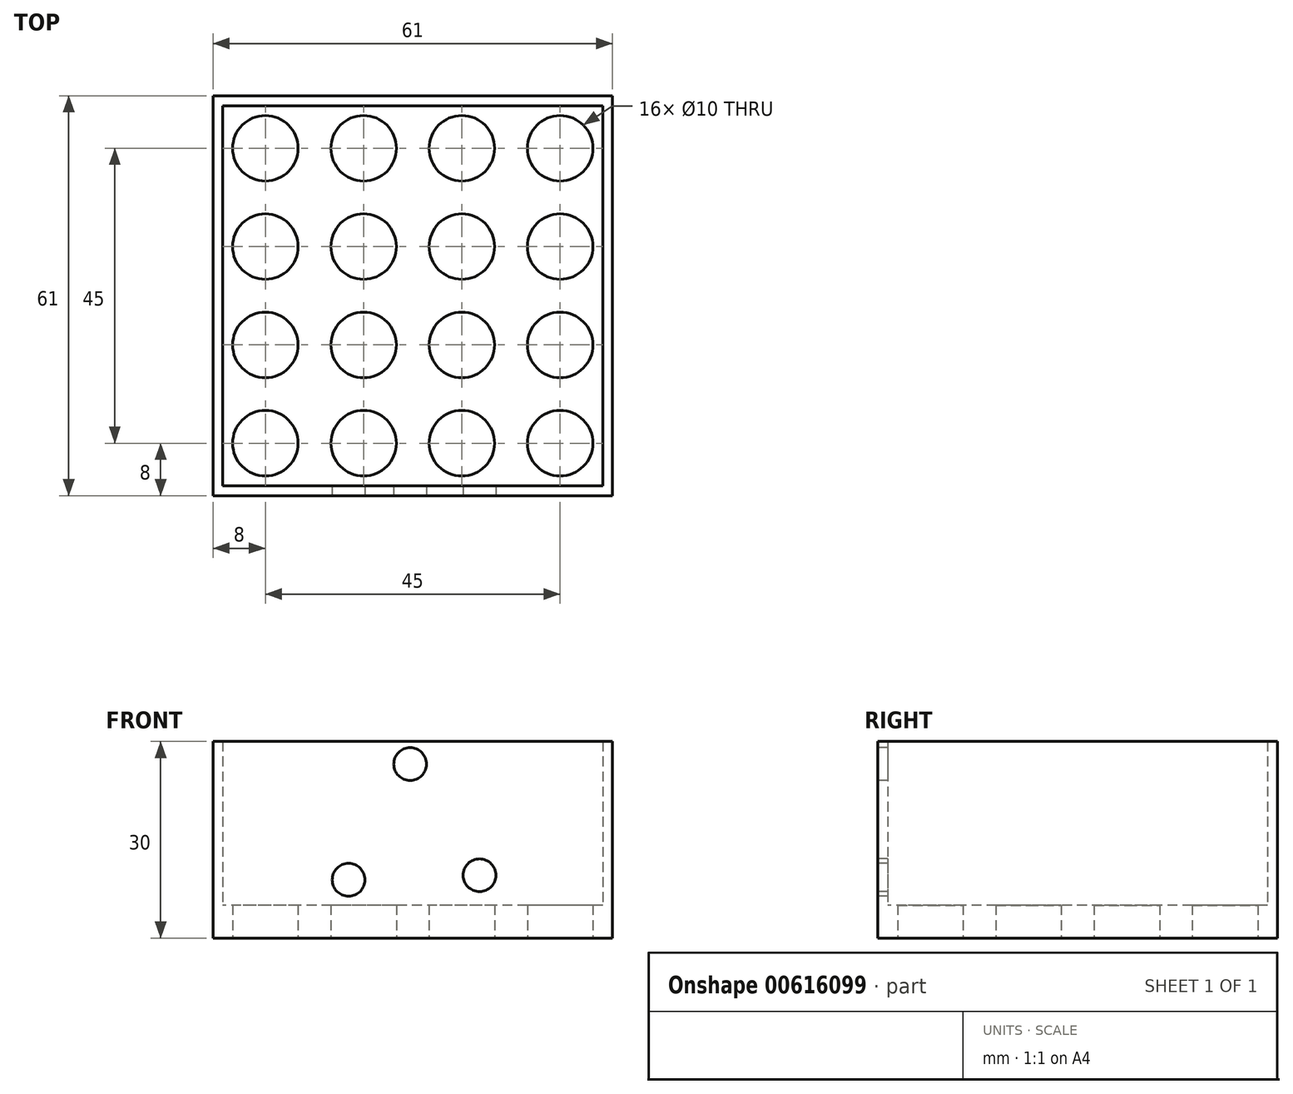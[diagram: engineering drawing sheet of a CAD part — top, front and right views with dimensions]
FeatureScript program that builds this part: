
annotation { "Feature Type Name" : "Feature", "Feature Type Description" : "" }
export const myFeature = defineFeature(function(context is Context, id is Id, definition is map)
    precondition{}
    {
        {
            var Q0;
            Q0=qCreatedBy(makeId("Top.planeOp"),FACE);
            var sketch = newSketch(context, id + "F0", { "sketchPlane" : qUnion([Q0])});
            skCircle(sketch, "E0", {"center": v(0, 0) * mm, "radius": 5 * mm});
            skCircle(sketch, "E1.0.1.0", {"center": v(0, 15) * mm, "radius": 5 * mm});
            skCircle(sketch, "E1.0.2.0", {"center": v(0, 30) * mm, "radius": 5 * mm});
            skCircle(sketch, "E1.0.3.0", {"center": v(0, 45) * mm, "radius": 5 * mm});
            skCircle(sketch, "E1.1.0.0", {"center": v(15, 0) * mm, "radius": 5 * mm});
            skCircle(sketch, "E1.1.1.0", {"center": v(15, 15) * mm, "radius": 5 * mm});
            skCircle(sketch, "E1.1.2.0", {"center": v(15, 30) * mm, "radius": 5 * mm});
            skCircle(sketch, "E1.1.3.0", {"center": v(15, 45) * mm, "radius": 5 * mm});
            skCircle(sketch, "E1.2.0.0", {"center": v(30, 0) * mm, "radius": 5 * mm});
            skCircle(sketch, "E1.2.1.0", {"center": v(30, 15) * mm, "radius": 5 * mm});
            skCircle(sketch, "E1.2.2.0", {"center": v(30, 30) * mm, "radius": 5 * mm});
            skCircle(sketch, "E1.2.3.0", {"center": v(30, 45) * mm, "radius": 5 * mm});
            skCircle(sketch, "E1.3.0.0", {"center": v(45, 0) * mm, "radius": 5 * mm});
            skCircle(sketch, "E1.3.1.0", {"center": v(45, 15) * mm, "radius": 5 * mm});
            skCircle(sketch, "E1.3.2.0", {"center": v(45, 30) * mm, "radius": 5 * mm});
            skCircle(sketch, "E1.3.3.0", {"center": v(45, 45) * mm, "radius": 5 * mm});
            skLineSegment(sketch, "E1.direction1", {"start": v(0, 0) * mm, "end": v(15, 0) * mm, "construction": true});
            skLineSegment(sketch, "E1.direction2", {"start": v(0, 0) * mm, "end": v(0, 15) * mm, "construction": true});
            skLineSegment(sketch, "E2.bottom", {"start": v(-8, 53) * mm, "end": v(53, 53) * mm});
            skLineSegment(sketch, "E2.top", {"start": v(-8, -8) * mm, "end": v(53, -8) * mm});
            skLineSegment(sketch, "E2.left", {"start": v(-8, 53) * mm, "end": v(-8, -8) * mm});
            skLineSegment(sketch, "E2.right", {"start": v(53, 53) * mm, "end": v(53, -8) * mm});
            skSolve(sketch);
        }
        {
            var Q0;
            Q0 = qSketchRegion(id + "F0", true);
            extrude(context, id + "F1", {"entities" : qUnion([Q0]), "depth" : 5 * mm, "offsetDistance" : 25 * mm});
        }
        {
            var Q0;
            Q0=makeQuery(id+"F1.opExtrude","CAP_FACE",FACE,{"disambiguationData":[OSD([sQuery(id+"F0.wireOp",EDGE,"E0"),sQuery(id+"F0.wireOp",EDGE,"E1.0.1.0"),sQuery(id+"F0.wireOp",EDGE,"E1.0.2.0"),sQuery(id+"F0.wireOp",EDGE,"E1.0.3.0"),sQuery(id+"F0.wireOp",EDGE,"E1.1.0.0"),sQuery(id+"F0.wireOp",EDGE,"E1.1.1.0"),sQuery(id+"F0.wireOp",EDGE,"E1.1.2.0"),sQuery(id+"F0.wireOp",EDGE,"E1.1.3.0"),sQuery(id+"F0.wireOp",EDGE,"E1.2.0.0"),sQuery(id+"F0.wireOp",EDGE,"E1.2.1.0"),sQuery(id+"F0.wireOp",EDGE,"E1.2.2.0"),sQuery(id+"F0.wireOp",EDGE,"E1.2.3.0"),sQuery(id+"F0.wireOp",EDGE,"E1.3.0.0"),sQuery(id+"F0.wireOp",EDGE,"E1.3.1.0"),sQuery(id+"F0.wireOp",EDGE,"E1.3.2.0"),sQuery(id+"F0.wireOp",EDGE,"E1.3.3.0"),sQuery(id+"F0.wireOp",EDGE,"E2.bottom"),sQuery(id+"F0.wireOp",EDGE,"E2.top"),sQuery(id+"F0.wireOp",EDGE,"E2.left"),sQuery(id+"F0.wireOp",EDGE,"E2.right")])],"isStart":false});
            var sketch = newSketch(context, id + "F2", { "sketchPlane" : qUnion([Q0])});
            skLineSegment(sketch, "E3.0", {"start": v(-6.5, 51.5) * mm, "end": v(-6.5, -6.5) * mm});
            skLineSegment(sketch, "E3.1", {"start": v(51.5, 51.5) * mm, "end": v(-6.5, 51.5) * mm});
            skLineSegment(sketch, "E3.2", {"start": v(51.5, -6.5) * mm, "end": v(51.5, 51.5) * mm});
            skLineSegment(sketch, "E3.3", {"start": v(-6.5, -6.5) * mm, "end": v(51.5, -6.5) * mm});
            skSolve(sketch);
        }
        {
            var Q0;
            Q0=makeQuery(id+"F2.imprint","IMPRINT",FACE,{"disambiguationData":[TD([[makeQuery(id+"F2.imprint","IMPRINT",EDGE,{"derivedFrom":sQuery(id+"F2.wireOp",EDGE,"E3.0")}),-1.0]])]});
            extrude(context, id + "F3", {"entities" : qUnion([Q0]), "operationType" : NewBodyOperationType.ADD, "depth" : 25 * mm, "offsetDistance" : 25 * mm});
        }
        {
            var Q0;
            {var subQ0=sQuery(id+"F0.wireOp",EDGE,"E2.top");Q0=makeQuery(id+"F3.boolean.opBoolean","MERGE",FACE,{"derivedFrom":[makeQuery(id+"F1.opExtrude","SWEPT_FACE",FACE,{"disambiguationData":[OSD([subQ0])]}),makeQuery(id+"F3.opExtrude","SWEPT_FACE",FACE,{"disambiguationData":[OSD([subQ0])]})]});}
            var sketch = newSketch(context, id + "F4", { "sketchPlane" : qUnion([Q0])});
            skCircle(sketch, "E4", {"center": v(22.1, 26.54) * mm, "radius": 2.5 * mm});
            skCircle(sketch, "E5.1.0", {"center": v(12.7, 8.88) * mm, "radius": 2.5 * mm});
            skCircle(sketch, "E5.2.0", {"center": v(32.7, 9.57) * mm, "radius": 2.5 * mm});
            skPoint(sketch, "E5.center", {"position": v(22.5, 15) * mm});
            skSolve(sketch);
        }
        {
            var Q0;
            Q0 = qSketchRegion(id + "F4", true);
            extrude(context, id + "F5", {"entities" : qUnion([Q0]), "operationType" : NewBodyOperationType.REMOVE, "endBound" : BoundingType.UP_TO_NEXT, "oppositeDirection" : true, "depth" : 25 * mm, "offsetDistance" : 25 * mm});
        }
    });
